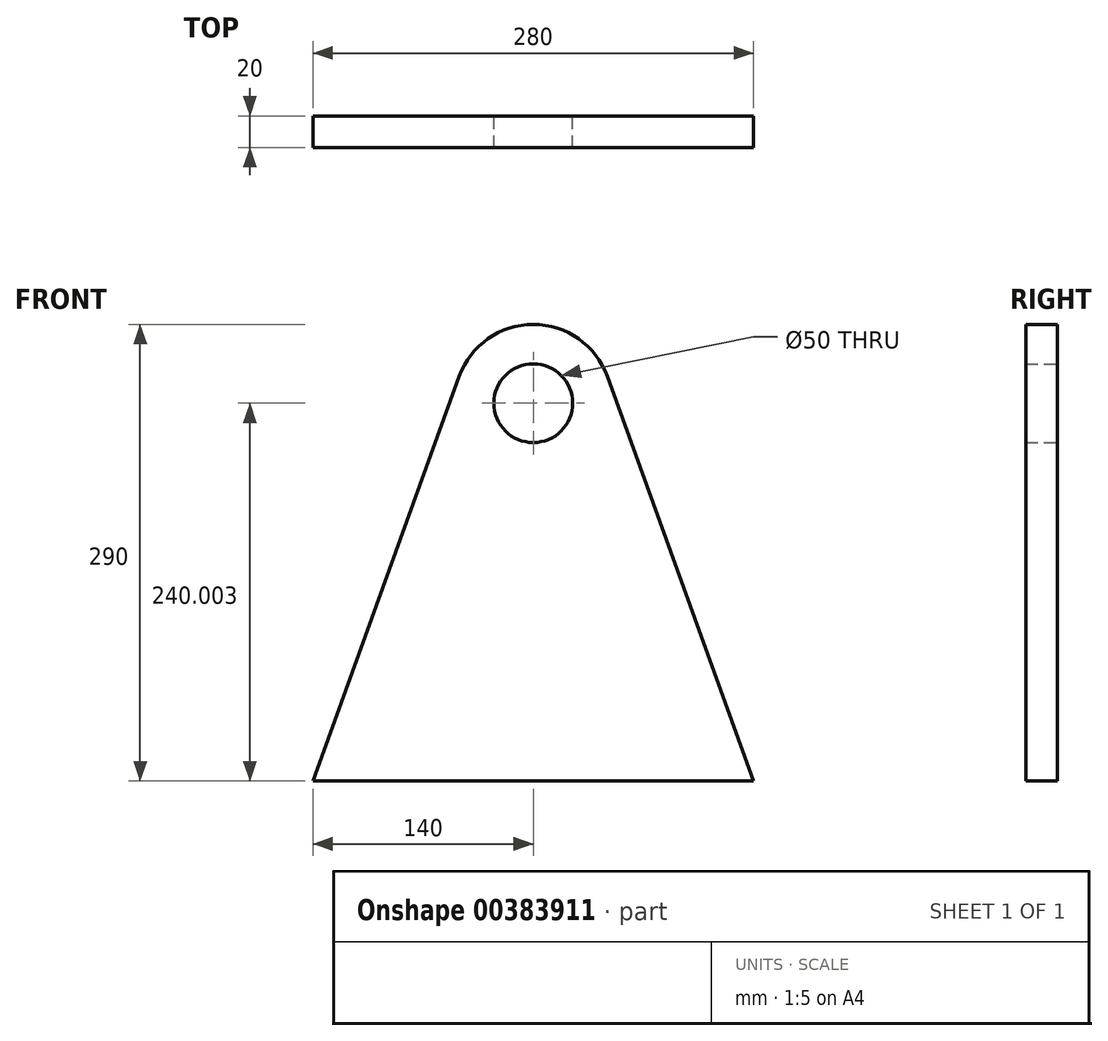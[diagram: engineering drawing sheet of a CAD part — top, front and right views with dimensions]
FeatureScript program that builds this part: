
annotation { "Feature Type Name" : "Feature", "Feature Type Description" : "" }
export const myFeature = defineFeature(function(context is Context, id is Id, definition is map)
    precondition{}
    {
        {
            var Q0;
            Q0=qCreatedBy(makeId("Front.planeOp"),FACE);
            var sketch = newSketch(context, id + "F0", { "sketchPlane" : qUnion([Q0])});
            skCircle(sketch, "E0", {"center": v(0, 188.34) * mm, "radius": 50 * mm});
            skCircle(sketch, "E1", {"center": v(0, 188.34) * mm, "radius": 25 * mm});
            skLineSegment(sketch, "E2", {"start": v(0, 188.34) * mm, "end": v(0, -51.66) * mm, "construction": true});
            skLineSegment(sketch, "E3", {"start": v(-140, -51.66) * mm, "end": v(140, -51.66) * mm});
            skLineSegment(sketch, "E4", {"start": v(-140, -51.66) * mm, "end": v(-47.02, 205.35) * mm});
            skLineSegment(sketch, "E5", {"start": v(140, -51.66) * mm, "end": v(47.02, 205.35) * mm});
            skSolve(sketch);
        }
        {
            var Q0;
            Q0=makeQuery(id+"F0.imprint","IMPRINT",FACE,{"disambiguationData":[TD([[makeQuery(id+"F0.imprint","IMPRINT",EDGE,{"derivedFrom":sQuery(id+"F0.wireOp",EDGE,"E3")}),1.0]])]});
            var Q1;
            Q1=makeQuery(id+"F0.imprint","IMPRINT",FACE,{"disambiguationData":[TD([[makeQuery(id+"F0.imprint","IMPRINT",EDGE,{"derivedFrom":sQuery(id+"F0.wireOp",EDGE,"E1")}),-1.0]])]});
            extrude(context, id + "F1", {"entities" : qUnion([Q0, Q1]), "depth" : 20 * mm});
        }
    });
